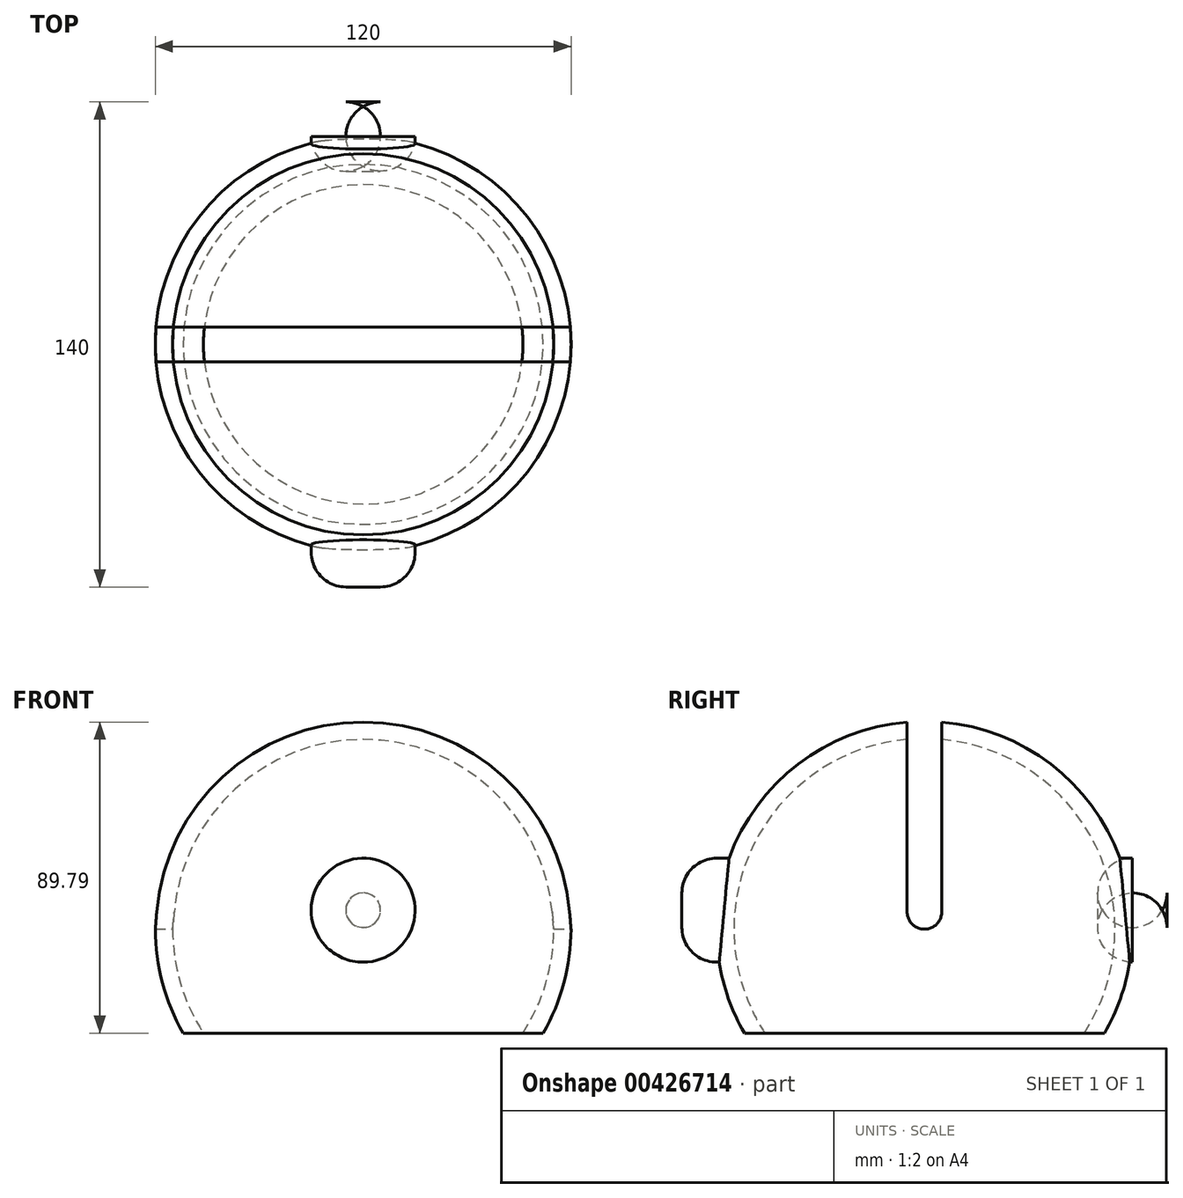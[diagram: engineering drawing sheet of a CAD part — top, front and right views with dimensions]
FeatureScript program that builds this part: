
annotation { "Feature Type Name" : "Feature", "Feature Type Description" : "" }
export const myFeature = defineFeature(function(context is Context, id is Id, definition is map)
    precondition{}
    {
        {
            var Q0;
            Q0=qCreatedBy(makeId("Top.planeOp"),FACE);
            var sketch = newSketch(context, id + "F0", { "sketchPlane" : qUnion([Q0])});
            skArc(sketch, "E0", {"start": v(60, 0) * mm, "mid": v(0, 60) * mm, "end": v(-60, 0) * mm});
            skArc(sketch, "E1.0", {"start": v(55, 0) * mm, "mid": v(0, 55) * mm, "end": v(-55, 0) * mm});
            skLineSegment(sketch, "E2", {"start": v(-60, 0) * mm, "end": v(-55, 0) * mm});
            skLineSegment(sketch, "E3.trimOffspring", {"start": v(55, 0) * mm, "end": v(60, 0) * mm});
            skLineSegment(sketch, "E4", {"start": v(-17.01, 0) * mm, "end": v(18, 0) * mm, "construction": true});
            skSolve(sketch);
        }
        {
            var Q0;
            Q0=makeQuery(id+"F0.imprint","IMPRINT",FACE,{"disambiguationData":[TD([[makeQuery(id+"F0.imprint","IMPRINT",EDGE,{"derivedFrom":sQuery(id+"F0.wireOp",EDGE,"E0")}),1.0]])]});
            var Q1;
            Q1 = qConstructionFilter(qBodyType(qCreatedBy(id + "F0" ,EDGE), BodyType.WIRE), ConstructionObject.NO);
            var Q2;
            Q2=sQuery(id+"F0.wireOp",EDGE,"E4");
            revolve(context, id + "F1", {"entities" : qUnion([Q0]), "surfaceEntities" : qUnion([Q1]), "axis" : qUnion([Q2]), "revolveType" : RevolveType.FULL});
        }
        {
            var Q0;
            Q0=qCreatedBy(makeId("Top.planeOp"),FACE);
            cPlane(context, id + "F2", {"entities" : qUnion([Q0]), "cplaneType" : CPlaneType.OFFSET, "offset" : 30 * mm, "oppositeDirection" : true, "width" : 150 * mm, "height" : 150 * mm});
        }
        {
            var Q0;
            Q0=qCreatedBy(id+"F2.planeOp",FACE);
            var sketch = newSketch(context, id + "F3", { "sketchPlane" : qUnion([Q0])});
            skCircle(sketch, "E5", {"center": v(0, 0) * mm, "radius": 100 * mm});
            skCircle(sketch, "E6", {"center": v(0, 0) * mm, "radius": 50 * mm, "construction": true});
            skSolve(sketch);
        }
        {
            var Q0;
            Q0 = qSketchRegion(id + "F3", true);
            extrude(context, id + "F4", {"entities" : qUnion([Q0]), "operationType" : NewBodyOperationType.REMOVE, "oppositeDirection" : true, "depth" : 40 * mm});
        }
        {
            var Q0;
            Q0=qCreatedBy(makeId("Right.planeOp"),FACE);
            var sketch = newSketch(context, id + "F5", { "sketchPlane" : qUnion([Q0])});
            skLineSegment(sketch, "E7.bottom", {"start": v(0, 68.9) * mm, "end": v(5, 68.9) * mm});
            skLineSegment(sketch, "E7.top", {"start": v(0, 0) * mm, "end": v(5, 0) * mm});
            skLineSegment(sketch, "E7.left", {"start": v(0, 68.9) * mm, "end": v(0, 0) * mm, "construction": true});
            skLineSegment(sketch, "E7.right", {"start": v(5, 68.9) * mm, "end": v(5, 0) * mm});
            skLineSegment(sketch, "E8.MirrorCS", {"start": v(0, 68.9) * mm, "end": v(-5, 68.9) * mm});
            skLineSegment(sketch, "E9.MirrorCS", {"start": v(-5, 68.9) * mm, "end": v(-5, 0) * mm});
            skLineSegment(sketch, "E10.MirrorCS", {"start": v(0, 0) * mm, "end": v(-5, 0) * mm});
            skSolve(sketch);
        }
        {
            var Q0;
            Q0 = qSketchRegion(id + "F5", true);
            extrude(context, id + "F6", {"entities" : qUnion([Q0]), "operationType" : NewBodyOperationType.REMOVE, "oppositeDirection" : true, "depth" : 79.1 * mm, "hasSecondDirection" : true, "secondDirectionOppositeDirection" : false, "secondDirectionDepth" : 91.5 * mm});
        }
        {
            var Q0;
            Q0=makeQuery(id+"F6.boolean.opBoolean","COPY",EDGE,{"disambiguationData":[OD(1.0)],"derivedFrom":makeQuery(id+"F6.opExtrude","SWEPT_EDGE",EDGE,{"disambiguationData":[OSD([sQuery(id+"F5.wireOp",EDGE,"E9.MirrorCS"),sQuery(id+"F5.wireOp",EDGE,"E10.MirrorCS")])]})});
            var Q1;
            Q1=makeQuery(id+"F6.boolean.opBoolean","COPY",EDGE,{"disambiguationData":[OD(1.0)],"derivedFrom":makeQuery(id+"F6.opExtrude","SWEPT_EDGE",EDGE,{"disambiguationData":[OSD([sQuery(id+"F5.wireOp",EDGE,"E7.top"),sQuery(id+"F5.wireOp",EDGE,"E7.right")])]})});
            var Q2;
            Q2=makeQuery(id+"F6.boolean.opBoolean","COPY",EDGE,{"disambiguationData":[OD(0.0)],"derivedFrom":makeQuery(id+"F6.opExtrude","SWEPT_EDGE",EDGE,{"disambiguationData":[OSD([sQuery(id+"F5.wireOp",EDGE,"E9.MirrorCS"),sQuery(id+"F5.wireOp",EDGE,"E10.MirrorCS")])]})});
            var Q3;
            Q3=makeQuery(id+"F6.boolean.opBoolean","COPY",EDGE,{"disambiguationData":[OD(0.0)],"derivedFrom":makeQuery(id+"F6.opExtrude","SWEPT_EDGE",EDGE,{"disambiguationData":[OSD([sQuery(id+"F5.wireOp",EDGE,"E7.top"),sQuery(id+"F5.wireOp",EDGE,"E7.right")])]})});
            fillet(context, id + "F7", {"entities" : qUnion([Q0, Q1, Q2, Q3]), "radius" : 5 * mm, "tangentPropagation" : true, "allowEdgeOverflow" : false});
        }
        {
            var Q0;
            Q0=qCreatedBy(makeId("Front.planeOp"),FACE);
            var sketch = newSketch(context, id + "F8", { "sketchPlane" : qUnion([Q0])});
            skCircle(sketch, "E11", {"center": v(0, 5.48) * mm, "radius": 15 * mm});
            skSolve(sketch);
        }
        {
            var Q0;
            Q0 = qSketchRegion(id + "F8", true);
            extrude(context, id + "F9", {"entities" : qUnion([Q0]), "operationType" : NewBodyOperationType.ADD, "depth" : 70 * mm, "hasSecondDirection" : true, "secondDirectionOppositeDirection" : true, "secondDirectionDepth" : 70 * mm});
        }
        {
            var Q0;
            Q0=makeQuery(id+"F9.opExtrude","CAP_EDGE",EDGE,{"disambiguationData":[OSD([sQuery(id+"F8.wireOp",EDGE,"E11")])],"isStart":false});
            var Q1;
            Q1=makeQuery(id+"F9.opExtrude","CAP_EDGE",EDGE,{"disambiguationData":[OSD([sQuery(id+"F8.wireOp",EDGE,"E11")])],"isStart":true});
            fillet(context, id + "F10", {"entities" : qUnion([Q0, Q1]), "radius" : 10 * mm, "tangentPropagation" : true, "allowEdgeOverflow" : false});
        }
        {
            var Q0;
            Q0=qCreatedBy(makeId("Top.planeOp"),FACE);
            var sketch = newSketch(context, id + "F11", { "sketchPlane" : qUnion([Q0])});
            skArc(sketch, "E12.0", {"start": v(55, 0) * mm, "mid": v(0, 55) * mm, "end": v(-55, 0) * mm});
            skLineSegment(sketch, "E13", {"start": v(55, 0) * mm, "end": v(-55, 0) * mm});
            skSolve(sketch);
        }
        {
            var Q0;
            Q0 = qSketchRegion(id + "F11", true);
            var Q1;
            Q1=sQuery(id+"F11.wireOp",EDGE,"E13");
            revolve(context, id + "F12", {"operationType" : NewBodyOperationType.REMOVE, "entities" : qUnion([Q0]), "axis" : qUnion([Q1]), "revolveType" : RevolveType.FULL, "oppositeDirection" : true});
        }
    });
